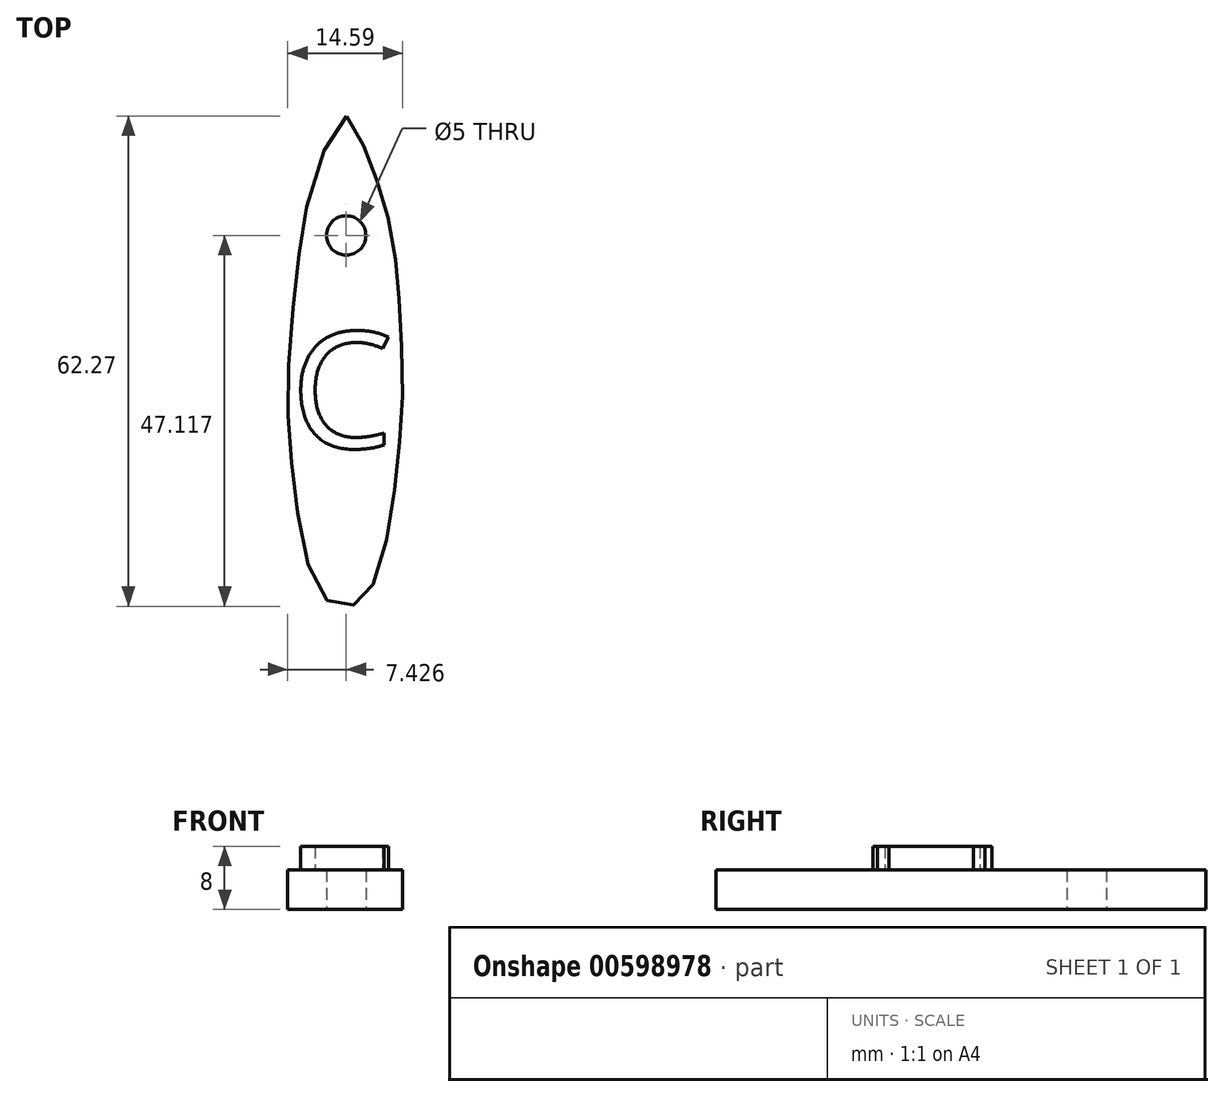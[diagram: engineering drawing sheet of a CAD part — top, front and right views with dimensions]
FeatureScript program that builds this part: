
annotation { "Feature Type Name" : "Feature", "Feature Type Description" : "" }
export const myFeature = defineFeature(function(context is Context, id is Id, definition is map)
    precondition{}
    {
        {
            var Q0;
            Q0=qCreatedBy(makeId("Top.planeOp"),FACE);
            var sketch = newSketch(context, id + "F0", { "sketchPlane" : qUnion([Q0])});
            skFitSpline(sketch, "E0", {"points": [v(-34.65, 65.8) * mm, v(-32.25, 61.3) * mm, v(-30.34, 56.32) * mm, v(-28.6, 48.87) * mm, v(-27.98, 42.28) * mm, v(-27.54, 32.23) * mm, v(-28.07, 23.02) * mm, v(-29.41, 12.85) * mm, v(-32.03, 5) * mm, v(-34.3, 3.58) * mm, v(-37.37, 4.47) * mm, v(-40.4, 12.76) * mm, v(-41.8, 23.5) * mm, v(-42.08, 33.2) * mm, v(-40.88, 46.68) * mm, v(-39.06, 56.84) * mm, v(-34.65, 65.8) * mm]});
            skCircle(sketch, "E1", {"center": v(-34.7, 50.65) * mm, "radius": 2.5 * mm});
            skSolve(sketch);
        }
        {
            var Q0;
            Q0=makeQuery(id+"F0.imprint","IMPRINT",FACE,{"disambiguationData":[TD([[makeQuery(id+"F0.imprint","IMPRINT",EDGE,{"derivedFrom":sQuery(id+"F0.wireOp",EDGE,"E0")}),-1.0]])]});
            extrude(context, id + "F1", {"entities" : qUnion([Q0]), "depth" : 5 * mm, "offsetDistance" : 25 * mm});
        }
        {
            var Q0;
            Q0=makeQuery(id+"F1.opExtrude","CAP_FACE",FACE,{"disambiguationData":[OSD([sQuery(id+"F0.wireOp",EDGE,"E0"),sQuery(id+"F0.wireOp",EDGE,"E1")])],"isStart":false});
            var sketch = newSketch(context, id + "F2", { "sketchPlane" : qUnion([Q0])});
            skText(sketch, "E2", { "text": "C\n", "fontName": "OpenSans-Regular.ttf"});
            const initialGuessF2  = {"E2": [-0.04173, 0.02366, 1, 0, 0.01483]};
            skSetInitialGuess(sketch, initialGuessF2);
            skSolve(sketch);
        }
        {
            var Q0;
            Q0 = qSketchRegion(id + "F2", true);
            extrude(context, id + "F3", {"entities" : qUnion([Q0]), "operationType" : NewBodyOperationType.ADD, "depth" : 3 * mm, "offsetDistance" : 25 * mm});
        }
    });
